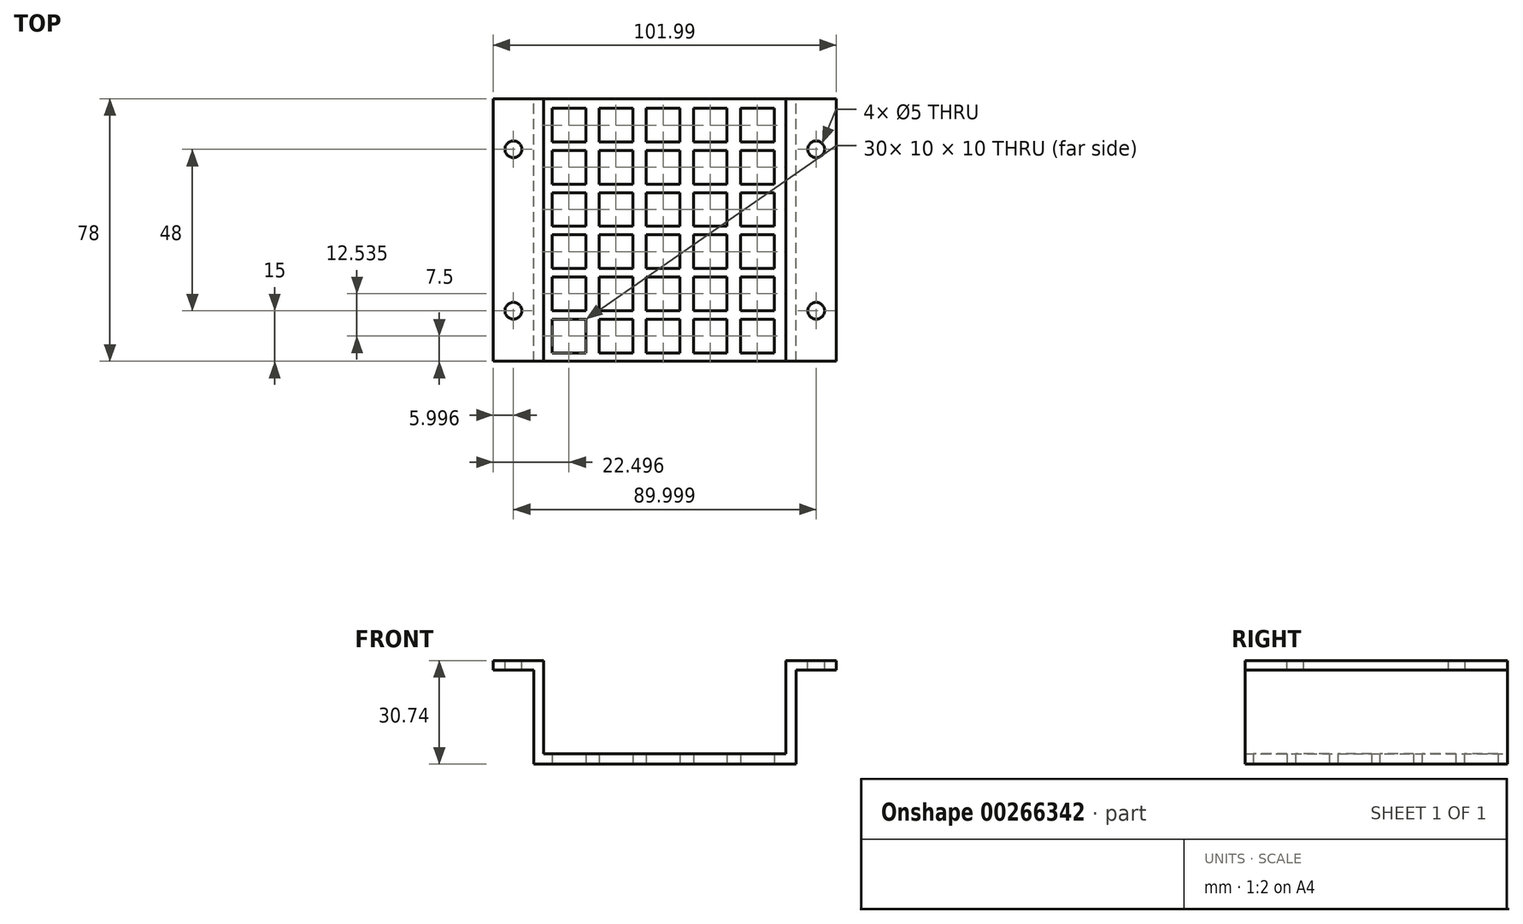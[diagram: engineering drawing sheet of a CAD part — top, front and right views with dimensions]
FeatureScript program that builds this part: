
annotation { "Feature Type Name" : "Feature", "Feature Type Description" : "" }
export const myFeature = defineFeature(function(context is Context, id is Id, definition is map)
    precondition{}
    {
        {
            var Q0;
            Q0=qCreatedBy(makeId("Front.planeOp"),FACE);
            var sketch = newSketch(context, id + "F0", { "sketchPlane" : qUnion([Q0])});
            skLineSegment(sketch, "E0", {"start": v(-2.97, -6.62) * mm, "end": v(-2.97, -9.62) * mm});
            skLineSegment(sketch, "E1", {"start": v(-2.97, -9.62) * mm, "end": v(36.03, -9.62) * mm});
            skLineSegment(sketch, "E2", {"start": v(36.03, -9.62) * mm, "end": v(36.03, 18.38) * mm});
            skLineSegment(sketch, "E3", {"start": v(36.03, 18.38) * mm, "end": v(48.02, 18.38) * mm});
            skLineSegment(sketch, "E4", {"start": v(48.02, 18.38) * mm, "end": v(48.02, 21.12) * mm});
            skLineSegment(sketch, "E5", {"start": v(48.02, 21.12) * mm, "end": v(33.02, 21.12) * mm});
            skLineSegment(sketch, "E6", {"start": v(33.02, 21.12) * mm, "end": v(33.02, -6.62) * mm});
            skLineSegment(sketch, "E7", {"start": v(33.02, -6.62) * mm, "end": v(-2.97, -6.62) * mm});
            skLineSegment(sketch, "E8.MirrorCS", {"start": v(-53.97, 18.38) * mm, "end": v(-53.97, 21.12) * mm});
            skLineSegment(sketch, "E9.MirrorCS", {"start": v(-41.97, -9.62) * mm, "end": v(-41.97, 18.38) * mm});
            skLineSegment(sketch, "E10.MirrorCS", {"start": v(-41.97, 18.38) * mm, "end": v(-53.97, 18.38) * mm});
            skLineSegment(sketch, "E11.MirrorCS", {"start": v(-53.97, 21.12) * mm, "end": v(-38.97, 21.12) * mm});
            skLineSegment(sketch, "E12.MirrorCS", {"start": v(-38.97, 21.12) * mm, "end": v(-38.97, -6.62) * mm});
            skLineSegment(sketch, "E13.MirrorCS", {"start": v(-2.97, -9.62) * mm, "end": v(-41.97, -9.62) * mm});
            skLineSegment(sketch, "E14.MirrorCS", {"start": v(-38.97, -6.62) * mm, "end": v(-2.97, -6.62) * mm});
            skPoint(sketch, "E15.MirrorCS.start.orphan", {"position": v(36.03, 18.38) * mm});
            skSolve(sketch);
        }
        {
            var Q0;
            Q0=qSketchRegion(id+"F0",true);
            extrude(context, id + "F1", {"entities" : qUnion([Q0]), "endBound" : BoundingType.SYMMETRIC, "depth" : 78 * mm});
        }
        {
            var Q0;
            Q0=makeQuery(id+"F1.opExtrude","SWEPT_FACE",FACE,{"disambiguationData":[OSD([sQuery(id+"F0.wireOp",EDGE,"E5")])]});
            var sketch = newSketch(context, id + "F2", { "sketchPlane" : qUnion([Q0])});
            skLineSegment(sketch, "E16", {"start": v(42.02, -39) * mm, "end": v(42.02, 39) * mm, "construction": true});
            skLineSegment(sketch, "E17.0.0", {"start": v(-38.97, 39) * mm, "end": v(-53.97, 39) * mm, "construction": true});
            skLineSegment(sketch, "E17.0.1", {"start": v(-53.97, 39) * mm, "end": v(-53.97, -39) * mm, "construction": true});
            skLineSegment(sketch, "E17.0.2", {"start": v(-53.97, -39) * mm, "end": v(-38.97, -39) * mm, "construction": true});
            skLineSegment(sketch, "E17.0.3", {"start": v(-38.97, -39) * mm, "end": v(-38.97, 39) * mm, "construction": true});
            skLineSegment(sketch, "E18", {"start": v(-47.97, 39) * mm, "end": v(-47.97, -39) * mm, "construction": true});
            skLineSegment(sketch, "E19", {"start": v(-53.97, -24) * mm, "end": v(48.02, -24) * mm, "construction": true});
            skLineSegment(sketch, "E20", {"start": v(48.02, 24) * mm, "end": v(-53.97, 24) * mm, "construction": true});
            skLineSegment(sketch, "E21", {"start": v(48.02, -24) * mm, "end": v(48.02, -39) * mm, "construction": true});
            skLineSegment(sketch, "E22", {"start": v(48.02, 39) * mm, "end": v(48.02, 24) * mm, "construction": true});
            skCircle(sketch, "E23", {"center": v(42.02, -24) * mm, "radius": 2.5 * mm});
            skCircle(sketch, "E24", {"center": v(42.02, 24) * mm, "radius": 2.5 * mm});
            skCircle(sketch, "E25", {"center": v(-47.97, 24) * mm, "radius": 2.5 * mm});
            skCircle(sketch, "E26", {"center": v(-47.97, -24) * mm, "radius": 2.5 * mm});
            skSolve(sketch);
        }
        {
            var Q0;
            Q0=qSketchRegion(id+"F2",true);
            extrude(context, id + "F3", {"entities" : qUnion([Q0]), "operationType" : NewBodyOperationType.REMOVE, "endBound" : BoundingType.UP_TO_NEXT, "oppositeDirection" : true, "depth" : 25 * mm});
        }
        {
            var Q0;
            Q0=makeQuery(id+"F1.opExtrude","SWEPT_FACE",FACE,{"disambiguationData":[OSD([sQuery(id+"F0.wireOp",EDGE,"E1"),sQuery(id+"F0.wireOp",EDGE,"E13.MirrorCS")])]});
            var sketch = newSketch(context, id + "F4", { "sketchPlane" : qUnion([Q0])});
            skLineSegment(sketch, "E27.bottom", {"start": v(-36.47, 36.5) * mm, "end": v(-26.47, 36.5) * mm});
            skLineSegment(sketch, "E27.top", {"start": v(-36.47, 26.5) * mm, "end": v(-26.47, 26.5) * mm});
            skLineSegment(sketch, "E27.left", {"start": v(-36.47, 36.5) * mm, "end": v(-36.47, 26.5) * mm});
            skLineSegment(sketch, "E27.right", {"start": v(-26.47, 36.5) * mm, "end": v(-26.47, 26.5) * mm});
            skLineSegment(sketch, "E28.1.0.0", {"start": v(-22.47, 36.5) * mm, "end": v(-12.47, 36.5) * mm});
            skLineSegment(sketch, "E28.1.0.1", {"start": v(-12.47, 36.5) * mm, "end": v(-12.47, 26.5) * mm});
            skLineSegment(sketch, "E28.1.0.2", {"start": v(-22.47, 36.5) * mm, "end": v(-22.47, 26.5) * mm});
            skLineSegment(sketch, "E28.1.0.3", {"start": v(-22.47, 26.5) * mm, "end": v(-12.47, 26.5) * mm});
            skLineSegment(sketch, "E28.2.0.0", {"start": v(-8.47, 36.5) * mm, "end": v(1.53, 36.5) * mm});
            skLineSegment(sketch, "E28.2.0.1", {"start": v(1.53, 36.5) * mm, "end": v(1.53, 26.5) * mm});
            skLineSegment(sketch, "E28.2.0.2", {"start": v(-8.47, 36.5) * mm, "end": v(-8.47, 26.5) * mm});
            skLineSegment(sketch, "E28.2.0.3", {"start": v(-8.47, 26.5) * mm, "end": v(1.53, 26.5) * mm});
            skLineSegment(sketch, "E28.3.0.0", {"start": v(5.53, 36.5) * mm, "end": v(15.53, 36.5) * mm});
            skLineSegment(sketch, "E28.3.0.1", {"start": v(15.53, 36.5) * mm, "end": v(15.53, 26.5) * mm});
            skLineSegment(sketch, "E28.3.0.2", {"start": v(5.53, 36.5) * mm, "end": v(5.53, 26.5) * mm});
            skLineSegment(sketch, "E28.3.0.3", {"start": v(5.53, 26.5) * mm, "end": v(15.53, 26.5) * mm});
            skLineSegment(sketch, "E28.4.0.0", {"start": v(19.53, 36.5) * mm, "end": v(29.53, 36.5) * mm});
            skLineSegment(sketch, "E28.4.0.1", {"start": v(29.53, 36.5) * mm, "end": v(29.53, 26.5) * mm});
            skLineSegment(sketch, "E28.4.0.2", {"start": v(19.53, 36.5) * mm, "end": v(19.53, 26.5) * mm});
            skLineSegment(sketch, "E28.4.0.3", {"start": v(19.53, 26.5) * mm, "end": v(29.53, 26.5) * mm});
            skLineSegment(sketch, "E28.direction1", {"start": v(-36.47, 36.5) * mm, "end": v(-22.47, 36.5) * mm, "construction": true});
            skLineSegment(sketch, "E29.1.0.0", {"start": v(5.53, 23.97) * mm, "end": v(5.53, 13.97) * mm});
            skLineSegment(sketch, "E29.1.0.1", {"start": v(5.53, 13.97) * mm, "end": v(15.53, 13.97) * mm});
            skLineSegment(sketch, "E29.1.0.2", {"start": v(19.53, 13.97) * mm, "end": v(29.53, 13.97) * mm});
            skLineSegment(sketch, "E29.1.0.3", {"start": v(15.53, 23.97) * mm, "end": v(15.53, 13.97) * mm});
            skLineSegment(sketch, "E29.1.0.4", {"start": v(29.53, 23.97) * mm, "end": v(29.53, 13.97) * mm});
            skLineSegment(sketch, "E29.1.0.5", {"start": v(-36.47, 13.97) * mm, "end": v(-26.47, 13.97) * mm});
            skLineSegment(sketch, "E29.1.0.6", {"start": v(-36.47, 23.97) * mm, "end": v(-36.47, 13.97) * mm});
            skLineSegment(sketch, "E29.1.0.7", {"start": v(-26.47, 23.97) * mm, "end": v(-26.47, 13.97) * mm});
            skLineSegment(sketch, "E29.1.0.8", {"start": v(-22.47, 23.97) * mm, "end": v(-12.47, 23.97) * mm});
            skLineSegment(sketch, "E29.1.0.9", {"start": v(-12.47, 23.97) * mm, "end": v(-12.47, 13.97) * mm});
            skLineSegment(sketch, "E29.1.0.10", {"start": v(-22.47, 23.97) * mm, "end": v(-22.47, 13.97) * mm});
            skLineSegment(sketch, "E29.1.0.11", {"start": v(-22.47, 13.97) * mm, "end": v(-12.47, 13.97) * mm});
            skLineSegment(sketch, "E29.1.0.12", {"start": v(-8.47, 23.97) * mm, "end": v(1.53, 23.97) * mm});
            skLineSegment(sketch, "E29.1.0.13", {"start": v(1.53, 23.97) * mm, "end": v(1.53, 13.97) * mm});
            skLineSegment(sketch, "E29.1.0.14", {"start": v(-8.47, 23.97) * mm, "end": v(-8.47, 13.97) * mm});
            skLineSegment(sketch, "E29.1.0.15", {"start": v(-8.47, 13.97) * mm, "end": v(1.53, 13.97) * mm});
            skLineSegment(sketch, "E29.1.0.16", {"start": v(5.53, 23.97) * mm, "end": v(15.53, 23.97) * mm});
            skLineSegment(sketch, "E29.1.0.17", {"start": v(19.53, 23.97) * mm, "end": v(29.53, 23.97) * mm});
            skLineSegment(sketch, "E29.1.0.18", {"start": v(-36.47, 23.97) * mm, "end": v(-22.47, 23.97) * mm, "construction": true});
            skLineSegment(sketch, "E29.1.0.19", {"start": v(19.53, 23.97) * mm, "end": v(19.53, 13.97) * mm});
            skLineSegment(sketch, "E29.1.0.20", {"start": v(-36.47, 23.97) * mm, "end": v(-26.47, 23.97) * mm});
            skLineSegment(sketch, "E29.2.0.0", {"start": v(5.53, 11.43) * mm, "end": v(5.53, 1.43) * mm});
            skLineSegment(sketch, "E29.2.0.1", {"start": v(5.53, 1.43) * mm, "end": v(15.53, 1.43) * mm});
            skLineSegment(sketch, "E29.2.0.2", {"start": v(19.53, 1.43) * mm, "end": v(29.53, 1.43) * mm});
            skLineSegment(sketch, "E29.2.0.3", {"start": v(15.53, 11.43) * mm, "end": v(15.53, 1.43) * mm});
            skLineSegment(sketch, "E29.2.0.4", {"start": v(29.53, 11.43) * mm, "end": v(29.53, 1.43) * mm});
            skLineSegment(sketch, "E29.2.0.5", {"start": v(-36.47, 1.43) * mm, "end": v(-26.47, 1.43) * mm});
            skLineSegment(sketch, "E29.2.0.6", {"start": v(-36.47, 11.43) * mm, "end": v(-36.47, 1.43) * mm});
            skLineSegment(sketch, "E29.2.0.7", {"start": v(-26.47, 11.43) * mm, "end": v(-26.47, 1.43) * mm});
            skLineSegment(sketch, "E29.2.0.8", {"start": v(-22.47, 11.43) * mm, "end": v(-12.47, 11.43) * mm});
            skLineSegment(sketch, "E29.2.0.9", {"start": v(-12.47, 11.43) * mm, "end": v(-12.47, 1.43) * mm});
            skLineSegment(sketch, "E29.2.0.10", {"start": v(-22.47, 11.43) * mm, "end": v(-22.47, 1.43) * mm});
            skLineSegment(sketch, "E29.2.0.11", {"start": v(-22.47, 1.43) * mm, "end": v(-12.47, 1.43) * mm});
            skLineSegment(sketch, "E29.2.0.12", {"start": v(-8.47, 11.43) * mm, "end": v(1.53, 11.43) * mm});
            skLineSegment(sketch, "E29.2.0.13", {"start": v(1.53, 11.43) * mm, "end": v(1.53, 1.43) * mm});
            skLineSegment(sketch, "E29.2.0.14", {"start": v(-8.47, 11.43) * mm, "end": v(-8.47, 1.43) * mm});
            skLineSegment(sketch, "E29.2.0.15", {"start": v(-8.47, 1.43) * mm, "end": v(1.53, 1.43) * mm});
            skLineSegment(sketch, "E29.2.0.16", {"start": v(5.53, 11.43) * mm, "end": v(15.53, 11.43) * mm});
            skLineSegment(sketch, "E29.2.0.17", {"start": v(19.53, 11.43) * mm, "end": v(29.53, 11.43) * mm});
            skLineSegment(sketch, "E29.2.0.18", {"start": v(-36.47, 11.43) * mm, "end": v(-22.47, 11.43) * mm, "construction": true});
            skLineSegment(sketch, "E29.2.0.19", {"start": v(19.53, 11.43) * mm, "end": v(19.53, 1.43) * mm});
            skLineSegment(sketch, "E29.2.0.20", {"start": v(-36.47, 11.43) * mm, "end": v(-26.47, 11.43) * mm});
            skLineSegment(sketch, "E29.3.0.0", {"start": v(5.53, -1.1) * mm, "end": v(5.53, -11.1) * mm});
            skLineSegment(sketch, "E29.3.0.1", {"start": v(5.53, -11.1) * mm, "end": v(15.53, -11.1) * mm});
            skLineSegment(sketch, "E29.3.0.2", {"start": v(19.53, -11.1) * mm, "end": v(29.53, -11.1) * mm});
            skLineSegment(sketch, "E29.3.0.3", {"start": v(15.53, -1.1) * mm, "end": v(15.53, -11.1) * mm});
            skLineSegment(sketch, "E29.3.0.4", {"start": v(29.53, -1.1) * mm, "end": v(29.53, -11.1) * mm});
            skLineSegment(sketch, "E29.3.0.5", {"start": v(-36.47, -11.1) * mm, "end": v(-26.47, -11.1) * mm});
            skLineSegment(sketch, "E29.3.0.6", {"start": v(-36.47, -1.1) * mm, "end": v(-36.47, -11.1) * mm});
            skLineSegment(sketch, "E29.3.0.7", {"start": v(-26.47, -1.1) * mm, "end": v(-26.47, -11.1) * mm});
            skLineSegment(sketch, "E29.3.0.8", {"start": v(-22.47, -1.1) * mm, "end": v(-12.47, -1.1) * mm});
            skLineSegment(sketch, "E29.3.0.9", {"start": v(-12.47, -1.1) * mm, "end": v(-12.47, -11.1) * mm});
            skLineSegment(sketch, "E29.3.0.10", {"start": v(-22.47, -1.1) * mm, "end": v(-22.47, -11.1) * mm});
            skLineSegment(sketch, "E29.3.0.11", {"start": v(-22.47, -11.1) * mm, "end": v(-12.47, -11.1) * mm});
            skLineSegment(sketch, "E29.3.0.12", {"start": v(-8.47, -1.1) * mm, "end": v(1.53, -1.1) * mm});
            skLineSegment(sketch, "E29.3.0.13", {"start": v(1.53, -1.1) * mm, "end": v(1.53, -11.1) * mm});
            skLineSegment(sketch, "E29.3.0.14", {"start": v(-8.47, -1.1) * mm, "end": v(-8.47, -11.1) * mm});
            skLineSegment(sketch, "E29.3.0.15", {"start": v(-8.47, -11.1) * mm, "end": v(1.53, -11.1) * mm});
            skLineSegment(sketch, "E29.3.0.16", {"start": v(5.53, -1.1) * mm, "end": v(15.53, -1.1) * mm});
            skLineSegment(sketch, "E29.3.0.17", {"start": v(19.53, -1.1) * mm, "end": v(29.53, -1.1) * mm});
            skLineSegment(sketch, "E29.3.0.18", {"start": v(-36.47, -1.1) * mm, "end": v(-22.47, -1.1) * mm, "construction": true});
            skLineSegment(sketch, "E29.3.0.19", {"start": v(19.53, -1.1) * mm, "end": v(19.53, -11.1) * mm});
            skLineSegment(sketch, "E29.3.0.20", {"start": v(-36.47, -1.1) * mm, "end": v(-26.47, -1.1) * mm});
            skLineSegment(sketch, "E29.4.0.0", {"start": v(5.53, -13.64) * mm, "end": v(5.53, -23.64) * mm});
            skLineSegment(sketch, "E29.4.0.1", {"start": v(5.53, -23.64) * mm, "end": v(15.53, -23.64) * mm});
            skLineSegment(sketch, "E29.4.0.2", {"start": v(19.53, -23.64) * mm, "end": v(29.53, -23.64) * mm});
            skLineSegment(sketch, "E29.4.0.3", {"start": v(15.53, -13.64) * mm, "end": v(15.53, -23.64) * mm});
            skLineSegment(sketch, "E29.4.0.4", {"start": v(29.53, -13.64) * mm, "end": v(29.53, -23.64) * mm});
            skLineSegment(sketch, "E29.4.0.5", {"start": v(-36.47, -23.64) * mm, "end": v(-26.47, -23.64) * mm});
            skLineSegment(sketch, "E29.4.0.6", {"start": v(-36.47, -13.64) * mm, "end": v(-36.47, -23.64) * mm});
            skLineSegment(sketch, "E29.4.0.7", {"start": v(-26.47, -13.64) * mm, "end": v(-26.47, -23.64) * mm});
            skLineSegment(sketch, "E29.4.0.8", {"start": v(-22.47, -13.64) * mm, "end": v(-12.47, -13.64) * mm});
            skLineSegment(sketch, "E29.4.0.9", {"start": v(-12.47, -13.64) * mm, "end": v(-12.47, -23.64) * mm});
            skLineSegment(sketch, "E29.4.0.10", {"start": v(-22.47, -13.64) * mm, "end": v(-22.47, -23.64) * mm});
            skLineSegment(sketch, "E29.4.0.11", {"start": v(-22.47, -23.64) * mm, "end": v(-12.47, -23.64) * mm});
            skLineSegment(sketch, "E29.4.0.12", {"start": v(-8.47, -13.64) * mm, "end": v(1.53, -13.64) * mm});
            skLineSegment(sketch, "E29.4.0.13", {"start": v(1.53, -13.64) * mm, "end": v(1.53, -23.64) * mm});
            skLineSegment(sketch, "E29.4.0.14", {"start": v(-8.47, -13.64) * mm, "end": v(-8.47, -23.64) * mm});
            skLineSegment(sketch, "E29.4.0.15", {"start": v(-8.47, -23.64) * mm, "end": v(1.53, -23.64) * mm});
            skLineSegment(sketch, "E29.4.0.16", {"start": v(5.53, -13.64) * mm, "end": v(15.53, -13.64) * mm});
            skLineSegment(sketch, "E29.4.0.17", {"start": v(19.53, -13.64) * mm, "end": v(29.53, -13.64) * mm});
            skLineSegment(sketch, "E29.4.0.18", {"start": v(-36.47, -13.64) * mm, "end": v(-22.47, -13.64) * mm, "construction": true});
            skLineSegment(sketch, "E29.4.0.19", {"start": v(19.53, -13.64) * mm, "end": v(19.53, -23.64) * mm});
            skLineSegment(sketch, "E29.4.0.20", {"start": v(-36.47, -13.64) * mm, "end": v(-26.47, -13.64) * mm});
            skLineSegment(sketch, "E29.direction1", {"start": v(-36.47, 26.5) * mm, "end": v(-36.47, 12.5) * mm, "construction": true});
            skLineSegment(sketch, "E30.0.5.0", {"start": v(5.53, -26.17) * mm, "end": v(5.53, -36.17) * mm});
            skLineSegment(sketch, "E30.3.5.0", {"start": v(5.53, -36.17) * mm, "end": v(15.53, -36.17) * mm});
            skLineSegment(sketch, "E30.6.5.0", {"start": v(19.53, -36.17) * mm, "end": v(29.53, -36.17) * mm});
            skLineSegment(sketch, "E30.9.5.0", {"start": v(15.53, -26.17) * mm, "end": v(15.53, -36.17) * mm});
            skLineSegment(sketch, "E30.12.5.0", {"start": v(29.53, -26.17) * mm, "end": v(29.53, -36.17) * mm});
            skLineSegment(sketch, "E30.15.5.0", {"start": v(-36.47, -36.17) * mm, "end": v(-26.47, -36.17) * mm});
            skLineSegment(sketch, "E30.18.5.0", {"start": v(-36.47, -26.17) * mm, "end": v(-36.47, -36.17) * mm});
            skLineSegment(sketch, "E30.21.5.0", {"start": v(-26.47, -26.17) * mm, "end": v(-26.47, -36.17) * mm});
            skLineSegment(sketch, "E30.24.5.0", {"start": v(-22.47, -26.17) * mm, "end": v(-12.47, -26.17) * mm});
            skLineSegment(sketch, "E30.27.5.0", {"start": v(-12.47, -26.17) * mm, "end": v(-12.47, -36.17) * mm});
            skLineSegment(sketch, "E30.30.5.0", {"start": v(-22.47, -26.17) * mm, "end": v(-22.47, -36.17) * mm});
            skLineSegment(sketch, "E30.33.5.0", {"start": v(-22.47, -36.17) * mm, "end": v(-12.47, -36.17) * mm});
            skLineSegment(sketch, "E30.36.5.0", {"start": v(-8.47, -26.17) * mm, "end": v(1.53, -26.17) * mm});
            skLineSegment(sketch, "E30.39.5.0", {"start": v(1.53, -26.17) * mm, "end": v(1.53, -36.17) * mm});
            skLineSegment(sketch, "E30.42.5.0", {"start": v(-8.47, -26.17) * mm, "end": v(-8.47, -36.17) * mm});
            skLineSegment(sketch, "E30.45.5.0", {"start": v(-8.47, -36.17) * mm, "end": v(1.53, -36.17) * mm});
            skLineSegment(sketch, "E30.48.5.0", {"start": v(5.53, -26.17) * mm, "end": v(15.53, -26.17) * mm});
            skLineSegment(sketch, "E30.51.5.0", {"start": v(19.53, -26.17) * mm, "end": v(29.53, -26.17) * mm});
            skLineSegment(sketch, "E30.54.5.0", {"start": v(-36.47, -26.17) * mm, "end": v(-22.47, -26.17) * mm, "construction": true});
            skLineSegment(sketch, "E30.57.5.0", {"start": v(19.53, -26.17) * mm, "end": v(19.53, -36.17) * mm});
            skLineSegment(sketch, "E30.60.5.0", {"start": v(-36.47, -26.17) * mm, "end": v(-26.47, -26.17) * mm});
            skSolve(sketch);
        }
        {
            var Q0;
            Q0=qSketchRegion(id+"F4",true);
            extrude(context, id + "F5", {"entities" : qUnion([Q0]), "operationType" : NewBodyOperationType.REMOVE, "endBound" : BoundingType.UP_TO_NEXT, "oppositeDirection" : true, "depth" : 25 * mm});
        }
    });
